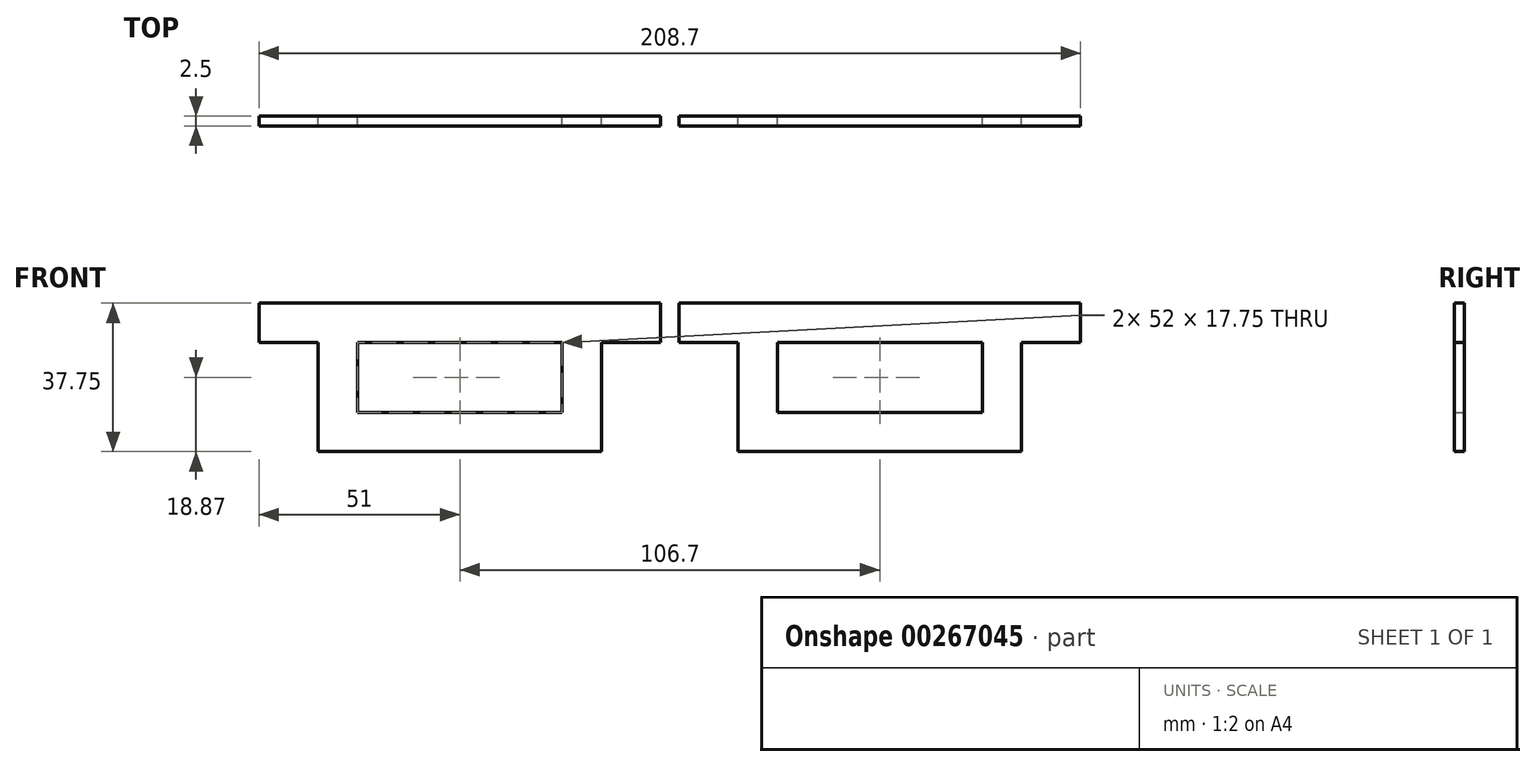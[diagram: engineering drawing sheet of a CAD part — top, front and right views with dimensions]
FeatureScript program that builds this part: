
annotation { "Feature Type Name" : "Feature", "Feature Type Description" : "" }
export const myFeature = defineFeature(function(context is Context, id is Id, definition is map)
    precondition{}
    {
        {
            var Q0;
            Q0=qCreatedBy(makeId("Front.planeOp"),FACE);
            var sketch = newSketch(context, id + "F0", { "sketchPlane" : qUnion([Q0])});
            skLineSegment(sketch, "E0", {"start": v(-36, -36.51) * mm, "end": v(36, -36.51) * mm});
            skLineSegment(sketch, "E1", {"start": v(36, -36.51) * mm, "end": v(36, -8.76) * mm});
            skLineSegment(sketch, "E2", {"start": v(36, -8.76) * mm, "end": v(51, -8.76) * mm});
            skLineSegment(sketch, "E3", {"start": v(-51, -8.76) * mm, "end": v(-36, -8.76) * mm});
            skLineSegment(sketch, "E4", {"start": v(-36, -8.76) * mm, "end": v(-36, -36.51) * mm});
            skLineSegment(sketch, "E5.0", {"start": v(-26, -26.51) * mm, "end": v(26, -26.51) * mm});
            skLineSegment(sketch, "E5.1", {"start": v(-26, -8.76) * mm, "end": v(-26, -26.51) * mm});
            skLineSegment(sketch, "E5.2", {"start": v(26, -26.51) * mm, "end": v(26, -8.76) * mm});
            skLineSegment(sketch, "E5.3", {"start": v(-51, 1.24) * mm, "end": v(-26, 1.24) * mm});
            skLineSegment(sketch, "E5.4", {"start": v(26, 1.24) * mm, "end": v(51, 1.24) * mm});
            skLineSegment(sketch, "E6.1.0.0", {"start": v(-132.7, -8.76) * mm, "end": v(-132.7, -26.51) * mm});
            skLineSegment(sketch, "E6.1.0.1", {"start": v(-132.7, -26.51) * mm, "end": v(-80.7, -26.51) * mm});
            skLineSegment(sketch, "E6.1.0.3", {"start": v(-142.7, -8.76) * mm, "end": v(-142.7, -36.51) * mm});
            skLineSegment(sketch, "E6.1.0.6", {"start": v(-70.7, -36.51) * mm, "end": v(-70.7, -8.76) * mm});
            skLineSegment(sketch, "E6.1.0.8", {"start": v(-142.7, -36.51) * mm, "end": v(-70.7, -36.51) * mm});
            skLineSegment(sketch, "E6.1.0.9", {"start": v(-80.7, -26.51) * mm, "end": v(-80.7, -8.76) * mm});
            skLineSegment(sketch, "E6.1.0.13", {"start": v(-70.7, -8.76) * mm, "end": v(-55.7, -8.76) * mm});
            skLineSegment(sketch, "E6.1.0.14", {"start": v(-157.7, -8.76) * mm, "end": v(-142.7, -8.76) * mm});
            skLineSegment(sketch, "E6.direction1", {"start": v(-36, -36.51) * mm, "end": v(-142.7, -36.51) * mm, "construction": true});
            skLineSegment(sketch, "E7", {"start": v(-55.7, -8.76) * mm, "end": v(-55.7, 1.24) * mm});
            skLineSegment(sketch, "E8", {"start": v(-51, -8.76) * mm, "end": v(-51, 1.24) * mm});
            skLineSegment(sketch, "E9", {"start": v(51, 1.24) * mm, "end": v(51, -8.76) * mm});
            skLineSegment(sketch, "E10", {"start": v(-157.7, -8.76) * mm, "end": v(-157.7, 1.24) * mm});
            skLineSegment(sketch, "E11", {"start": v(-157.7, 1.24) * mm, "end": v(-55.7, 1.24) * mm});
            skLineSegment(sketch, "E12", {"start": v(-132.7, -8.76) * mm, "end": v(-80.7, -8.76) * mm});
            skPoint(sketch, "E13.orphan", {"position": v(-132.7, 1.24) * mm});
            skPoint(sketch, "E14.orphan", {"position": v(-80.7, 1.24) * mm});
            skPoint(sketch, "E15.orphan", {"position": v(-41, 1.24) * mm});
            skPoint(sketch, "E16.orphan", {"position": v(41, 1.24) * mm});
            skLineSegment(sketch, "E17", {"start": v(-26, 1.24) * mm, "end": v(26, 1.24) * mm});
            skLineSegment(sketch, "E18", {"start": v(26, -8.76) * mm, "end": v(-26, -8.76) * mm});
            skSolve(sketch);
        }
        {
            var Q0;
            Q0=makeQuery(id+"F0.imprint","IMPRINT",FACE,{"disambiguationData":[TD([[makeQuery(id+"F0.imprint","IMPRINT",EDGE,{"derivedFrom":sQuery(id+"F0.wireOp",EDGE,"E0")}),1.0]])]});
            var Q1;
            Q1=makeQuery(id+"F0.imprint","IMPRINT",FACE,{"disambiguationData":[TD([[makeQuery(id+"F0.imprint","IMPRINT",EDGE,{"derivedFrom":sQuery(id+"F0.wireOp",EDGE,"E6.1.0.0")}),-1.0]])]});
            extrude(context, id + "F1", {"entities" : qUnion([Q0, Q1]), "depth" : 2.5 * mm});
        }
    });
